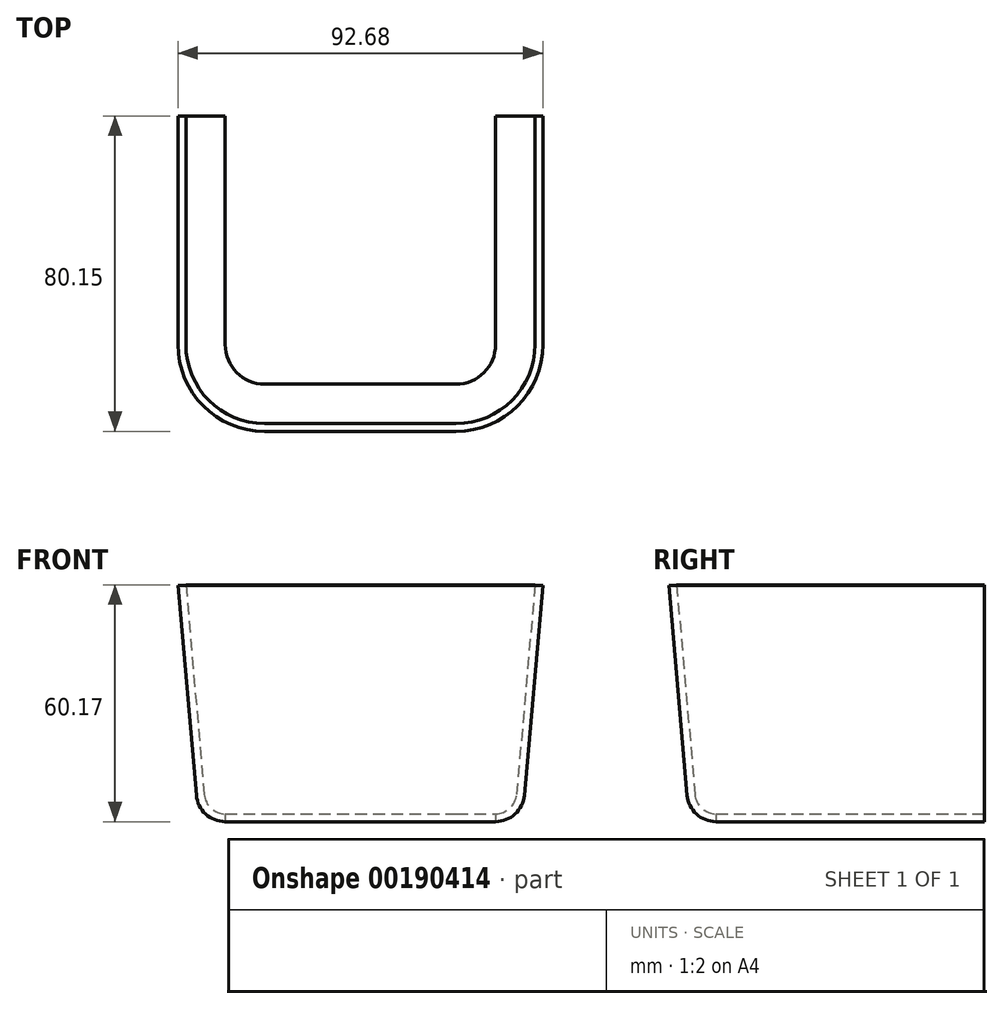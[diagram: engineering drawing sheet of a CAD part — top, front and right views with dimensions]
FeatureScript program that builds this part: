
annotation { "Feature Type Name" : "Feature", "Feature Type Description" : "" }
export const myFeature = defineFeature(function(context is Context, id is Id, definition is map)
    precondition{}
    {
        {
            var Q0;
            Q0=qCreatedBy(makeId("Top.planeOp"),FACE);
            var sketch = newSketch(context, id + "F0", { "sketchPlane" : qUnion([Q0])});
            skLineSegment(sketch, "E0.bottom", {"start": v(24.34, 68.15) * mm, "end": v(-24.34, 68.15) * mm, "construction": true});
            skLineSegment(sketch, "E0.top", {"start": v(24.34, -68.15) * mm, "end": v(-24.34, -68.15) * mm});
            skLineSegment(sketch, "E0.left", {"start": v(34.34, 0) * mm, "end": v(34.34, -58.15) * mm});
            skLineSegment(sketch, "E0.right", {"start": v(-34.34, 0) * mm, "end": v(-34.34, -58.15) * mm});
            skPoint(sketch, "E0.middle", {"position": v(0, 0) * mm});
            skPoint(sketch, "E1.visualSharp", {"position": v(-34.34, 68.15) * mm});
            skArc(sketch, "E1.filletArc", {"start": v(-24.34, 68.15) * mm, "mid": v(-31.4, 65.22) * mm, "end": v(-34.34, 58.15) * mm, "construction": true});
            skPoint(sketch, "E2.visualSharp", {"position": v(34.34, 68.15) * mm});
            skArc(sketch, "E2.filletArc", {"start": v(34.34, 58.15) * mm, "mid": v(31.4, 65.22) * mm, "end": v(24.34, 68.15) * mm, "construction": true});
            skPoint(sketch, "E3.visualSharp", {"position": v(34.34, -68.15) * mm});
            skArc(sketch, "E3.filletArc", {"start": v(24.34, -68.15) * mm, "mid": v(31.4, -65.22) * mm, "end": v(34.34, -58.15) * mm});
            skPoint(sketch, "E4.visualSharp", {"position": v(-34.34, -68.15) * mm});
            skArc(sketch, "E4.filletArc", {"start": v(-34.34, -58.15) * mm, "mid": v(-31.4, -65.22) * mm, "end": v(-24.34, -68.15) * mm});
            skLineSegment(sketch, "E5", {"start": v(-34.34, 0) * mm, "end": v(34.34, 0) * mm});
            skSolve(sketch);
        }
        {
            var Q0;
            Q0=qCreatedBy(makeId("Top.planeOp"),FACE);
            cPlane(context, id + "F1", {"entities" : qUnion([Q0]), "cplaneType" : CPlaneType.OFFSET, "offset" : 60 * mm, "width" : 150 * mm, "height" : 150 * mm});
        }
        {
            var Q0;
            Q0=qCreatedBy(id+"F1.planeOp",FACE);
            var sketch = newSketch(context, id + "F2", { "sketchPlane" : qUnion([Q0])});
            skArc(sketch, "E6.0", {"start": v(-24.34, 80.15) * mm, "mid": v(-39.9, 73.7) * mm, "end": v(-46.34, 58.15) * mm, "construction": true});
            skLineSegment(sketch, "E6.1", {"start": v(24.34, 80.15) * mm, "end": v(-24.34, 80.15) * mm, "construction": true});
            skLineSegment(sketch, "E6.2", {"start": v(-46.34, 0) * mm, "end": v(-46.34, -58.15) * mm});
            skArc(sketch, "E6.3", {"start": v(46.34, 58.15) * mm, "mid": v(39.9, 73.7) * mm, "end": v(24.34, 80.15) * mm, "construction": true});
            skArc(sketch, "E6.4", {"start": v(-46.34, -58.15) * mm, "mid": v(-39.9, -73.7) * mm, "end": v(-24.34, -80.15) * mm});
            skLineSegment(sketch, "E6.5", {"start": v(24.34, -80.15) * mm, "end": v(-24.34, -80.15) * mm});
            skArc(sketch, "E6.6", {"start": v(24.34, -80.15) * mm, "mid": v(39.9, -73.7) * mm, "end": v(46.34, -58.15) * mm});
            skLineSegment(sketch, "E6.7", {"start": v(46.34, 0) * mm, "end": v(46.34, -58.15) * mm});
            skLineSegment(sketch, "E7", {"start": v(-46.34, 0) * mm, "end": v(46.34, 0) * mm});
            skSolve(sketch);
        }
        {
            var Q0;
            Q0=qCreatedBy(makeId("Front.planeOp"),FACE);
            var sketch = newSketch(context, id + "F3", { "sketchPlane" : qUnion([Q0])});
            skLineSegment(sketch, "E8", {"start": v(-46.34, 60) * mm, "end": v(-41.68, 6.72) * mm});
            skArc(sketch, "E9", {"start": v(-41.68, 6.72) * mm, "mid": v(-39.31, 1.94) * mm, "end": v(-34.34, 0) * mm});
            skArc(sketch, "E10.0", {"start": v(-39.68, 6.9) * mm, "mid": v(-37.96, 3.41) * mm, "end": v(-34.34, 2) * mm});
            skLineSegment(sketch, "E10.1", {"start": v(-44.35, 60.17) * mm, "end": v(-39.68, 6.9) * mm});
            skLineSegment(sketch, "E11", {"start": v(-46.34, 60) * mm, "end": v(-44.35, 60.17) * mm});
            skLineSegment(sketch, "E12", {"start": v(-34.34, 2) * mm, "end": v(-34.34, 0) * mm});
            skSolve(sketch);
        }
        {
            var Q0;
            Q0=makeQuery(id+"F3.imprint","IMPRINT",FACE,{"disambiguationData":[TD([[makeQuery(id+"F3.imprint","IMPRINT",EDGE,{"derivedFrom":sQuery(id+"F3.wireOp",EDGE,"E8")}),1.0]])]});
            var Q1;
            Q1=sQuery(id+"F2.wireOp",EDGE,"E6.2");
            var Q2;
            Q2=sQuery(id+"F2.wireOp",EDGE,"E6.4");
            var Q3;
            Q3=sQuery(id+"F2.wireOp",EDGE,"E6.5");
            var Q4;
            Q4=sQuery(id+"F2.wireOp",EDGE,"E6.6");
            var Q5;
            Q5=sQuery(id+"F2.wireOp",EDGE,"E6.7");
            sweep(context, id + "F4", {"profiles" : qUnion([Q0]), "path" : qUnion([Q1, Q2, Q3, Q4, Q5])});
        }
    });
